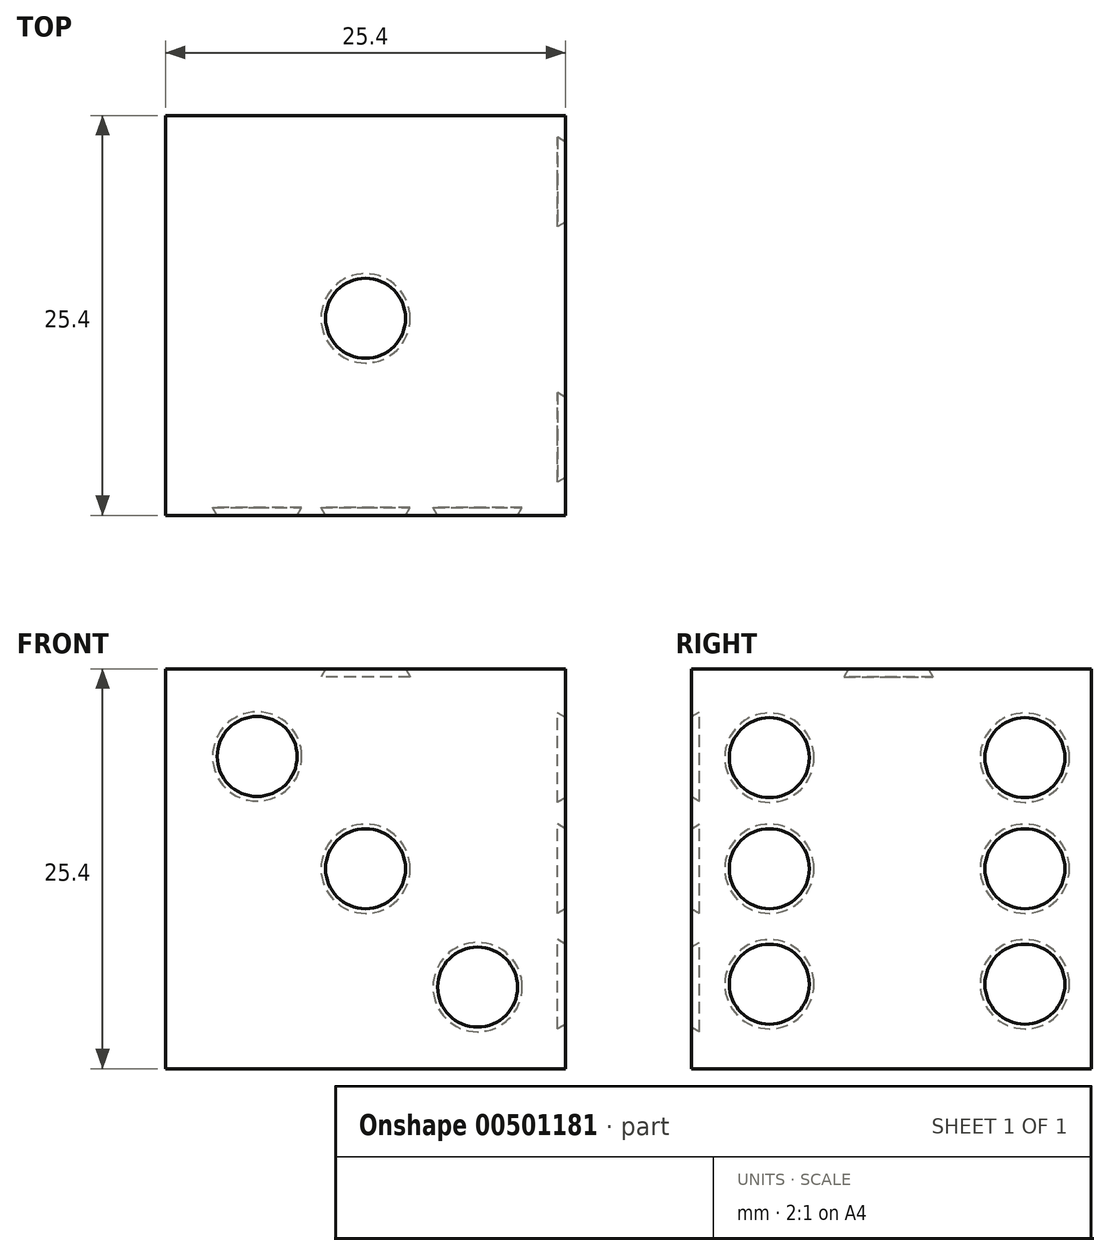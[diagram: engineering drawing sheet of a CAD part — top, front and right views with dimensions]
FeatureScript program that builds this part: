
annotation { "Feature Type Name" : "Feature", "Feature Type Description" : "" }
export const myFeature = defineFeature(function(context is Context, id is Id, definition is map)
    precondition{}
    {
        {
            var Q0;
            Q0=qCreatedBy(makeId("Front.planeOp"),FACE);
            var sketch = newSketch(context, id + "F0", { "sketchPlane" : qUnion([Q0])});
            skLineSegment(sketch, "E0.bottom", {"start": v(12.7, 12.7) * mm, "end": v(-12.7, 12.7) * mm});
            skLineSegment(sketch, "E0.top", {"start": v(12.7, -12.7) * mm, "end": v(-12.7, -12.7) * mm});
            skLineSegment(sketch, "E0.left", {"start": v(12.7, 12.7) * mm, "end": v(12.7, -12.7) * mm});
            skLineSegment(sketch, "E0.right", {"start": v(-12.7, 12.7) * mm, "end": v(-12.7, -12.7) * mm});
            skPoint(sketch, "E0.middle", {"position": v(0, 0) * mm});
            skSolve(sketch);
        }
        {
            var Q0;
            Q0=makeQuery(id+"F0.imprint","IMPRINT",FACE,{"disambiguationData":[TD([[makeQuery(id+"F0.imprint","IMPRINT",EDGE,{"derivedFrom":sQuery(id+"F0.wireOp",EDGE,"E0.bottom")}),1.0]])]});
            extrude(context, id + "F1", {"entities" : qUnion([Q0]), "depth" : 25.4 * mm});
        }
        {
            var Q0;
            Q0=makeQuery(id+"F1.opExtrude","SWEPT_FACE",FACE,{"disambiguationData":[OSD([sQuery(id+"F0.wireOp",EDGE,"E0.bottom")])]});
            var sketch = newSketch(context, id + "F2", { "sketchPlane" : qUnion([Q0])});
            skCircle(sketch, "E1", {"center": v(0, -12.89) * mm, "radius": 2.54 * mm});
            skSolve(sketch);
        }
        {
            var Q0;
            Q0=makeQuery(id+"F2.imprint","IMPRINT",FACE,{"disambiguationData":[TD([[makeQuery(id+"F2.imprint","IMPRINT",EDGE,{"derivedFrom":sQuery(id+"F2.wireOp",EDGE,"E1")}),1.0]])]});
            extrude(context, id + "F3", {"entities" : qUnion([Q0]), "operationType" : NewBodyOperationType.REMOVE, "oppositeDirection" : true, "depth" : 0.5 * mm, "hasDraft" : true, "draftAngle" : 30 * degree});
        }
        {
            var Q0;
            Q0=makeQuery(id+"F1.opExtrude","CAP_FACE",FACE,{"disambiguationData":[OSD([sQuery(id+"F0.wireOp",EDGE,"E0.bottom"),sQuery(id+"F0.wireOp",EDGE,"E0.top"),sQuery(id+"F0.wireOp",EDGE,"E0.left"),sQuery(id+"F0.wireOp",EDGE,"E0.right")])],"isStart":false});
            var sketch = newSketch(context, id + "F4", { "sketchPlane" : qUnion([Q0])});
            skCircle(sketch, "E2", {"center": v(0, 0) * mm, "radius": 2.54 * mm});
            skCircle(sketch, "E3", {"center": v(7.11, -7.52) * mm, "radius": 2.54 * mm});
            skCircle(sketch, "E4", {"center": v(-6.89, 7.13) * mm, "radius": 2.54 * mm});
            skSolve(sketch);
        }
        {
            var Q0;
            Q0=makeQuery(id+"F4.imprint","IMPRINT",FACE,{"disambiguationData":[TD([[makeQuery(id+"F4.imprint","IMPRINT",EDGE,{"derivedFrom":sQuery(id+"F4.wireOp",EDGE,"E4")}),1.0]])]});
            var Q1;
            Q1=makeQuery(id+"F4.imprint","IMPRINT",FACE,{"disambiguationData":[TD([[makeQuery(id+"F4.imprint","IMPRINT",EDGE,{"derivedFrom":sQuery(id+"F4.wireOp",EDGE,"E2")}),1.0]])]});
            var Q2;
            Q2=makeQuery(id+"F4.imprint","IMPRINT",FACE,{"disambiguationData":[TD([[makeQuery(id+"F4.imprint","IMPRINT",EDGE,{"derivedFrom":sQuery(id+"F4.wireOp",EDGE,"E3")}),1.0]])]});
            extrude(context, id + "F5", {"entities" : qUnion([Q0, Q1, Q2]), "operationType" : NewBodyOperationType.REMOVE, "oppositeDirection" : true, "depth" : 0.5 * mm, "hasDraft" : true, "draftAngle" : 30 * degree});
        }
        {
            var Q0;
            Q0=makeQuery(id+"F1.opExtrude","SWEPT_FACE",FACE,{"disambiguationData":[OSD([sQuery(id+"F0.wireOp",EDGE,"E0.left")])]});
            var sketch = newSketch(context, id + "F6", { "sketchPlane" : qUnion([Q0])});
            skCircle(sketch, "E5", {"center": v(-20.45, 7.05) * mm, "radius": 2.54 * mm});
            skCircle(sketch, "E6", {"center": v(-20.45, 0) * mm, "radius": 2.54 * mm});
            skCircle(sketch, "E7", {"center": v(-20.45, -7.34) * mm, "radius": 2.54 * mm});
            skCircle(sketch, "E8", {"center": v(-4.22, 7.05) * mm, "radius": 2.54 * mm});
            skCircle(sketch, "E9", {"center": v(-4.22, 0) * mm, "radius": 2.54 * mm});
            skCircle(sketch, "E10", {"center": v(-4.22, -7.34) * mm, "radius": 2.54 * mm});
            skSolve(sketch);
        }
        {
            var Q0;
            Q0=makeQuery(id+"F6.imprint","IMPRINT",FACE,{"disambiguationData":[TD([[makeQuery(id+"F6.imprint","IMPRINT",EDGE,{"derivedFrom":sQuery(id+"F6.wireOp",EDGE,"E5")}),1.0]])]});
            var Q1;
            Q1=makeQuery(id+"F6.imprint","IMPRINT",FACE,{"disambiguationData":[TD([[makeQuery(id+"F6.imprint","IMPRINT",EDGE,{"derivedFrom":sQuery(id+"F6.wireOp",EDGE,"E6")}),1.0]])]});
            var Q2;
            Q2=makeQuery(id+"F6.imprint","IMPRINT",FACE,{"disambiguationData":[TD([[makeQuery(id+"F6.imprint","IMPRINT",EDGE,{"derivedFrom":sQuery(id+"F6.wireOp",EDGE,"E7")}),1.0]])]});
            var Q3;
            Q3=makeQuery(id+"F6.imprint","IMPRINT",FACE,{"disambiguationData":[TD([[makeQuery(id+"F6.imprint","IMPRINT",EDGE,{"derivedFrom":sQuery(id+"F6.wireOp",EDGE,"E10")}),1.0]])]});
            var Q4;
            Q4=makeQuery(id+"F6.imprint","IMPRINT",FACE,{"disambiguationData":[TD([[makeQuery(id+"F6.imprint","IMPRINT",EDGE,{"derivedFrom":sQuery(id+"F6.wireOp",EDGE,"E9")}),1.0]])]});
            var Q5;
            Q5=makeQuery(id+"F6.imprint","IMPRINT",FACE,{"disambiguationData":[TD([[makeQuery(id+"F6.imprint","IMPRINT",EDGE,{"derivedFrom":sQuery(id+"F6.wireOp",EDGE,"E8")}),1.0]])]});
            extrude(context, id + "F7", {"entities" : qUnion([Q0, Q1, Q2, Q3, Q4, Q5]), "operationType" : NewBodyOperationType.REMOVE, "oppositeDirection" : true, "depth" : 0.5 * mm, "hasDraft" : true, "draftAngle" : 30 * degree});
        }
    });
